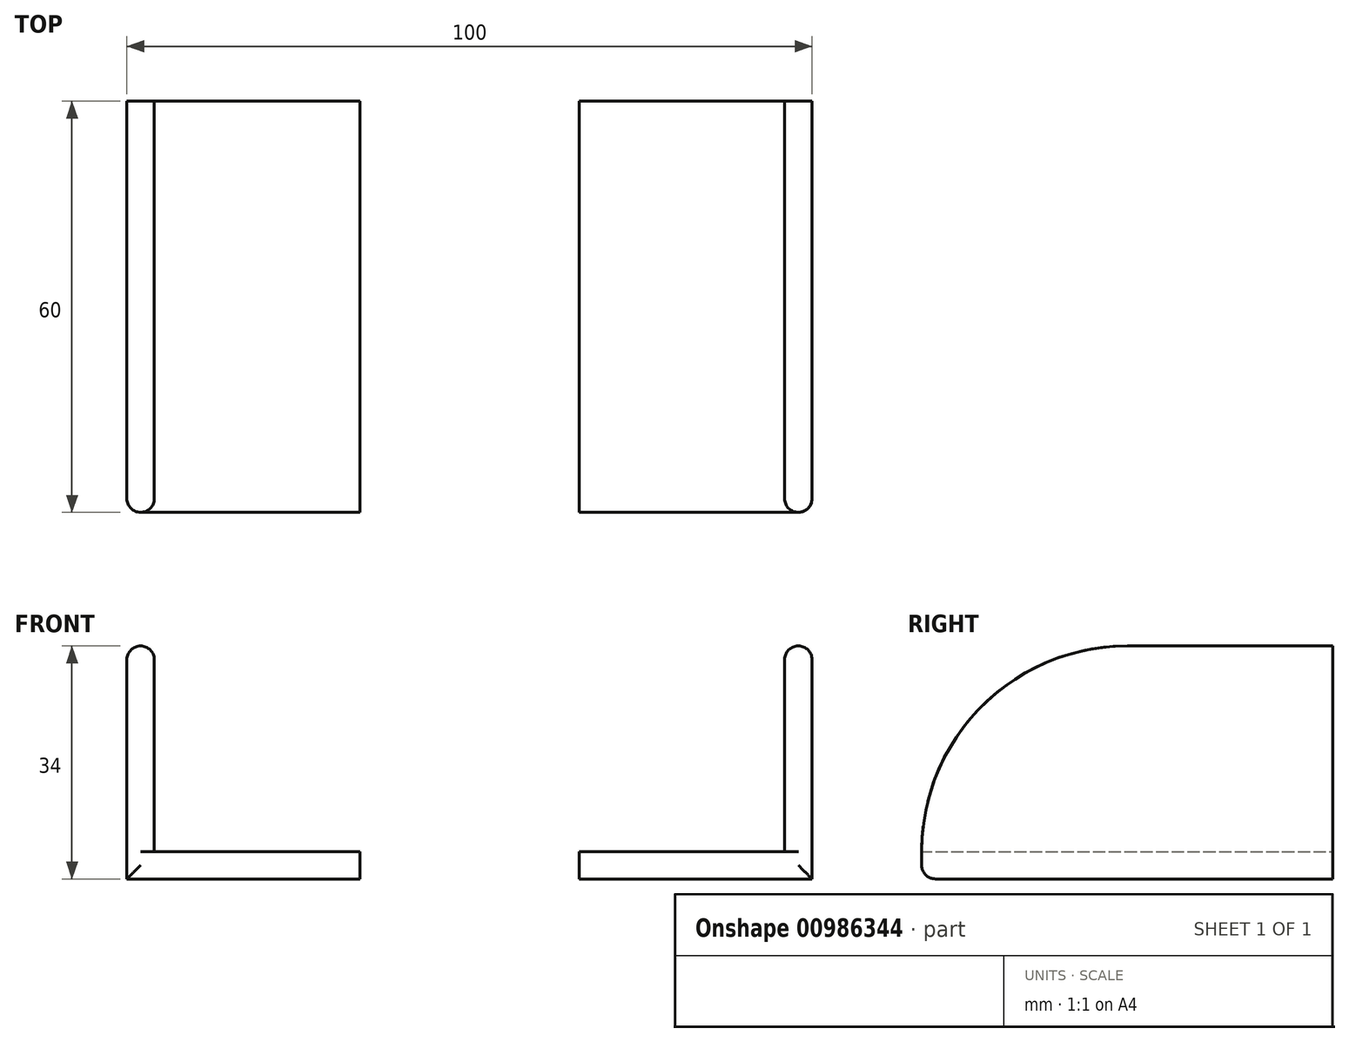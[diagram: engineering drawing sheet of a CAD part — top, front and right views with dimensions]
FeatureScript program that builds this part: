
annotation { "Feature Type Name" : "Feature", "Feature Type Description" : "" }
export const myFeature = defineFeature(function(context is Context, id is Id, definition is map)
    precondition{}
    {
        {
            var Q0;
            Q0=qCreatedBy(makeId("Front.planeOp"),FACE);
            var sketch = newSketch(context, id + "F0", { "sketchPlane" : qUnion([Q0])});
            skLineSegment(sketch, "E0", {"start": v(0, 0) * mm, "end": v(0, 34) * mm});
            skLineSegment(sketch, "E1", {"start": v(0, 0) * mm, "end": v(34, 0) * mm});
            skLineSegment(sketch, "E2", {"start": v(34, 0) * mm, "end": v(34, 4) * mm});
            skLineSegment(sketch, "E3", {"start": v(34, 4) * mm, "end": v(4, 4) * mm});
            skLineSegment(sketch, "E4", {"start": v(4, 4) * mm, "end": v(4, 34) * mm});
            skLineSegment(sketch, "E5", {"start": v(4, 34) * mm, "end": v(0, 34) * mm});
            skSolve(sketch);
        }
        {
            var Q0;
            Q0=qSketchRegion(id+"F0",true);
            extrude(context, id + "F1", {"entities" : qUnion([Q0]), "depth" : 60 * mm, "offsetDistance" : 25 * mm});
        }
        {
            var Q0;
            Q0=qCreatedBy(makeId("Right.planeOp"),FACE);
            cPlane(context, id + "F2", {"entities" : qUnion([Q0]), "cplaneType" : CPlaneType.OFFSET, "offset" : 50 * mm, "width" : 150 * mm, "height" : 150 * mm});
        }
        {
            var Q0;
            Q0=makeQuery(id+"F1.opExtrude","SWEPT_BODY",BODY,{"disambiguationData":[OSD([sQuery(id+"F0.wireOp",EDGE,"E0"),sQuery(id+"F0.wireOp",EDGE,"E1"),sQuery(id+"F0.wireOp",EDGE,"E2"),sQuery(id+"F0.wireOp",EDGE,"E3"),sQuery(id+"F0.wireOp",EDGE,"E4"),sQuery(id+"F0.wireOp",EDGE,"E5")])]});
            var Q1;
            Q1=qCreatedBy(id+"F2.planeOp",FACE);
            mirror(context, id + "F3", {"entities" : qUnion([Q0]), "mirrorPlane" : qUnion([Q1])});
        }
        {
            var Q0;
            Q0=makeQuery(id+"F1.opExtrude","CAP_EDGE",EDGE,{"disambiguationData":[OSD([sQuery(id+"F0.wireOp",EDGE,"E5")])],"isStart":false});
            var Q1;
            Q1=makeQuery(id+"F3.opPattern","COPY",EDGE,{"derivedFrom":makeQuery(id+"F1.opExtrude","CAP_EDGE",EDGE,{"disambiguationData":[OSD([sQuery(id+"F0.wireOp",EDGE,"E5")])],"isStart":false}),"instanceName":"1"});
            fillet(context, id + "F4", {"entities" : qUnion([Q0, Q1]), "radius" : 30 * mm, "tangentPropagation" : true, "allowEdgeOverflow" : false});
        }
        {
            var Q0;
            Q0=makeQuery(id+"F1.opExtrude","SWEPT_EDGE",EDGE,{"disambiguationData":[OSD([sQuery(id+"F0.wireOp",EDGE,"E0"),sQuery(id+"F0.wireOp",EDGE,"E5")])]});
            var Q1;
            Q1=makeQuery(id+"F4.opFillet","BLEND_EDGE",EDGE,{"blendedFrom":[makeQuery(id+"F1.opExtrude","CAP_EDGE",EDGE,{"disambiguationData":[OSD([sQuery(id+"F0.wireOp",EDGE,"E5")])],"isStart":false}),makeQuery(id+"F1.opExtrude","SWEPT_FACE",FACE,{"disambiguationData":[OSD([sQuery(id+"F0.wireOp",EDGE,"E0")])]})],"blendedInto":[makeQuery(id+"F1.opExtrude","SWEPT_FACE",FACE,{"disambiguationData":[OSD([sQuery(id+"F0.wireOp",EDGE,"E0")])]})]});
            var Q2;
            Q2=makeQuery(id+"F4.opFillet","BLEND_EDGE",EDGE,{"blendedFrom":[makeQuery(id+"F3.opPattern","COPY",EDGE,{"derivedFrom":makeQuery(id+"F1.opExtrude","CAP_EDGE",EDGE,{"disambiguationData":[OSD([sQuery(id+"F0.wireOp",EDGE,"E5")])],"isStart":false}),"instanceName":"1"}),makeQuery(id+"F3.opPattern","COPY",FACE,{"derivedFrom":makeQuery(id+"F1.opExtrude","SWEPT_FACE",FACE,{"disambiguationData":[OSD([sQuery(id+"F0.wireOp",EDGE,"E0")])]}),"instanceName":"1"})],"blendedInto":[makeQuery(id+"F3.opPattern","COPY",FACE,{"derivedFrom":makeQuery(id+"F1.opExtrude","SWEPT_FACE",FACE,{"disambiguationData":[OSD([sQuery(id+"F0.wireOp",EDGE,"E0")])]}),"instanceName":"1"})]});
            var Q3;
            Q3=makeQuery(id+"F1.opExtrude","SWEPT_EDGE",EDGE,{"disambiguationData":[OSD([sQuery(id+"F0.wireOp",EDGE,"E4"),sQuery(id+"F0.wireOp",EDGE,"E5")])]});
            var Q4;
            Q4=makeQuery(id+"F4.opFillet","BLEND_EDGE",EDGE,{"blendedFrom":[makeQuery(id+"F3.opPattern","COPY",EDGE,{"derivedFrom":makeQuery(id+"F1.opExtrude","CAP_EDGE",EDGE,{"disambiguationData":[OSD([sQuery(id+"F0.wireOp",EDGE,"E5")])],"isStart":false}),"instanceName":"1"}),makeQuery(id+"F3.opPattern","COPY",FACE,{"derivedFrom":makeQuery(id+"F1.opExtrude","SWEPT_FACE",FACE,{"disambiguationData":[OSD([sQuery(id+"F0.wireOp",EDGE,"E4")])]}),"instanceName":"1"})],"blendedInto":[makeQuery(id+"F3.opPattern","COPY",FACE,{"derivedFrom":makeQuery(id+"F1.opExtrude","SWEPT_FACE",FACE,{"disambiguationData":[OSD([sQuery(id+"F0.wireOp",EDGE,"E4")])]}),"instanceName":"1"})]});
            var Q5;
            Q5=makeQuery(id+"F1.opExtrude","CAP_EDGE",EDGE,{"disambiguationData":[OSD([sQuery(id+"F0.wireOp",EDGE,"E1")])],"isStart":false});
            var Q6;
            Q6=makeQuery(id+"F3.opPattern","COPY",EDGE,{"derivedFrom":makeQuery(id+"F1.opExtrude","CAP_EDGE",EDGE,{"disambiguationData":[OSD([sQuery(id+"F0.wireOp",EDGE,"E1")])],"isStart":false}),"instanceName":"1"});
            fillet(context, id + "F5", {"entities" : qUnion([Q0, Q1, Q2, Q3, Q4, Q5, Q6]), "radius" : 2 * mm, "tangentPropagation" : true, "allowEdgeOverflow" : false});
        }
    });
